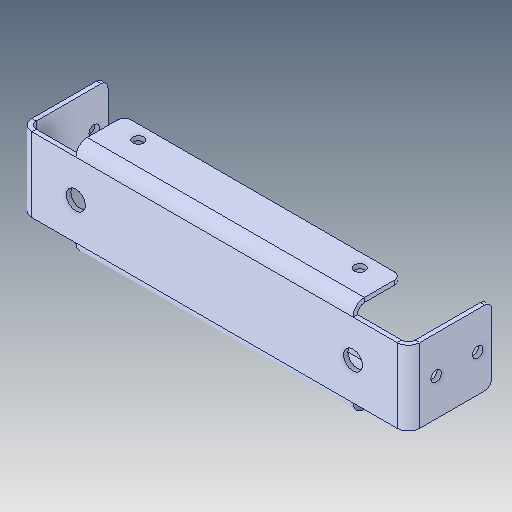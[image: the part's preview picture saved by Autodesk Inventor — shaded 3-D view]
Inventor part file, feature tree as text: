
AUTODESK INVENTOR PART (.ipt)
format: ipt  version: 2023.5 (Build 275446000, 446)  size: 133,632 bytes
history: native  units: in
note: dims shown in document units (in); Inventor stores cm internally (conversion verified against a paired STEP export)
features: fillet x1
ambient origin geometry x8: Origin, YZ Plane, XZ Plane, XY Plane, X Axis, Y Axis, Z Axis, Center Point
bodies: Solid1 (feature_tree)
feature tree (1):
  fillet  "Fillet1"  [1 undecoded]
note: 1 required parameter value undecoded (feature->parameter linkage not recoverable at this tier; creation-order binding heuristic only, values carry confidence <= 0.55)
